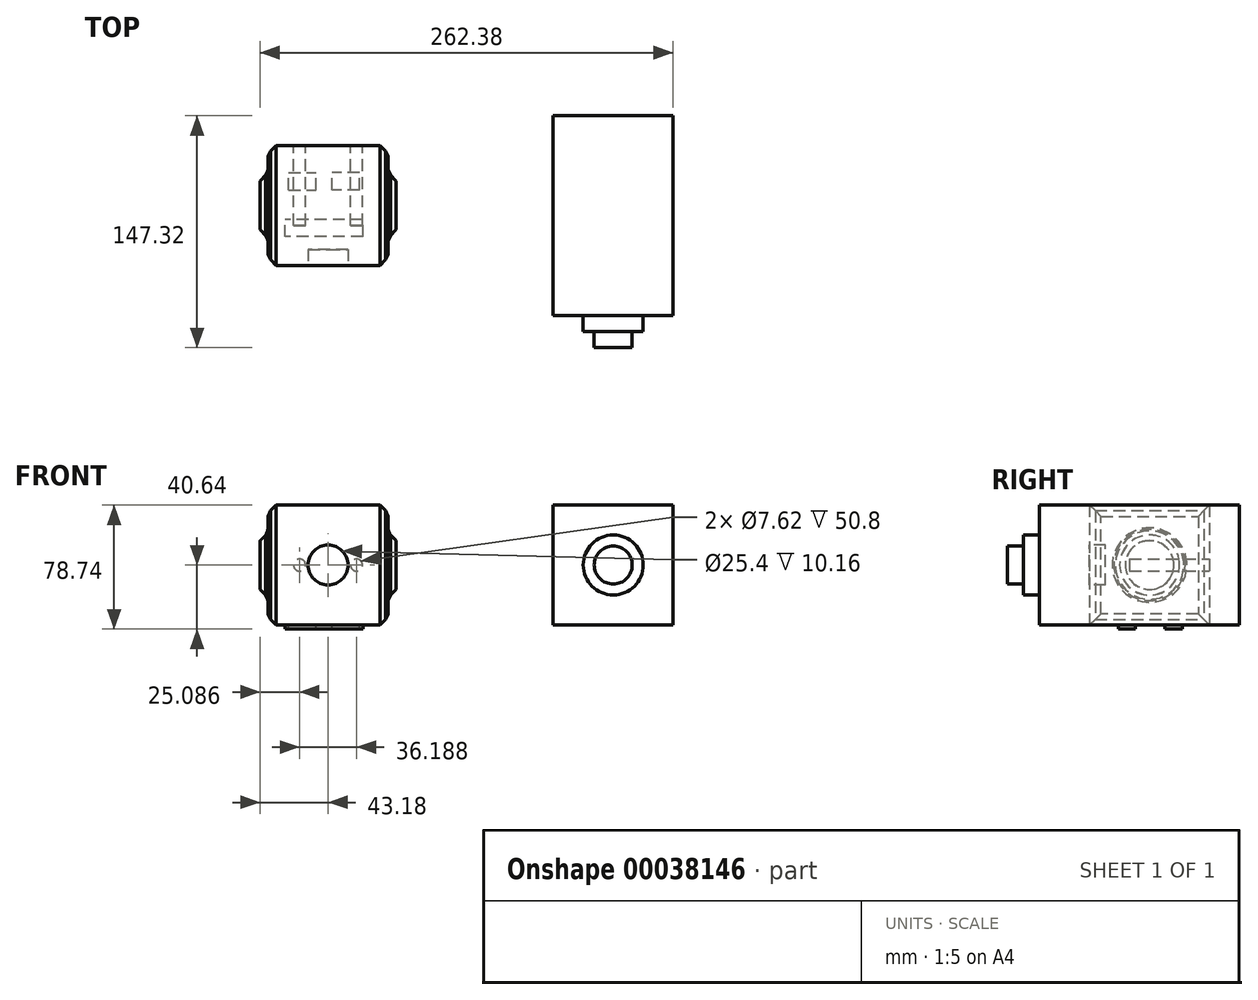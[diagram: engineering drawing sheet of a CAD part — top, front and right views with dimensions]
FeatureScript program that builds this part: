
annotation { "Feature Type Name" : "Feature", "Feature Type Description" : "" }
export const myFeature = defineFeature(function(context is Context, id is Id, definition is map)
    precondition{}
    {
        {
            var Q0;
            Q0=qCreatedBy(makeId("Top.planeOp"),FACE);
            var sketch = newSketch(context, id + "F0", { "sketchPlane" : qUnion([Q0])});
            skLineSegment(sketch, "E0.rect.bottom", {"start": v(-38.1, -38.1) * mm, "end": v(38.1, -38.1) * mm});
            skLineSegment(sketch, "E0.rect.top", {"start": v(-38.1, 38.1) * mm, "end": v(38.1, 38.1) * mm});
            skLineSegment(sketch, "E0.rect.left", {"start": v(-38.1, -38.1) * mm, "end": v(-38.1, -12.7) * mm});
            skLineSegment(sketch, "E0.rect.right", {"start": v(38.1, -38.1) * mm, "end": v(38.1, -12.7) * mm});
            skPoint(sketch, "E0.rect.middle", {"position": v(0, 0) * mm});
            skPoint(sketch, "E1", {"position": v(-38.1, -12.7) * mm});
            skPoint(sketch, "E2.endSnap0", {"position": v(-38.1, 0) * mm});
            skPoint(sketch, "E2.start.orphan", {"position": v(-38.1, 0) * mm});
            skLineSegment(sketch, "E3.trimOffspring", {"start": v(-38.1, 38.1) * mm, "end": v(-38.1, 38.1) * mm});
            skPoint(sketch, "E4.orphan", {"position": v(0, 38.1) * mm});
            skLineSegment(sketch, "E5.trimOffspring", {"start": v(38.1, 38.1) * mm, "end": v(38.1, 38.1) * mm});
            skPoint(sketch, "E6.end.orphan", {"position": v(0, -38.1) * mm});
            skPoint(sketch, "E7.rect.right.end.orphan", {"position": v(-50.16, 8.42) * mm});
            skPoint(sketch, "E8.orphan", {"position": v(-50.16, -8.42) * mm});
            skLineSegment(sketch, "E9", {"start": v(-38.1, 38.1) * mm, "end": v(-38.1, -12.7) * mm});
            skLineSegment(sketch, "E10", {"start": v(38.1, 38.1) * mm, "end": v(38.1, -12.7) * mm});
            skSolve(sketch);
        }
        {
            var Q0;
            Q0 = qSketchRegion(id + "F0", true);
            extrude(context, id + "F1", {"entities" : qUnion([Q0]), "depth" : 76.2 * mm});
        }
        {
            var Q0;
            Q0=makeQuery(id+"F1.opExtrude","SWEPT_FACE",FACE,{"disambiguationData":[OSD([sQuery(id+"F0.wireOp",EDGE,"E0.rect.right"),sQuery(id+"F0.wireOp",EDGE,"E5.trimOffspring"),sQuery(id+"F0.wireOp",EDGE,"E10")])]});
            var sketch = newSketch(context, id + "F2", { "sketchPlane" : qUnion([Q0])});
            skLineSegment(sketch, "E11.rect.bottom", {"start": v(-25.4, 12.7) * mm, "end": v(25.4, 12.7) * mm});
            skLineSegment(sketch, "E11.rect.top", {"start": v(-25.4, 63.5) * mm, "end": v(25.4, 63.5) * mm});
            skLineSegment(sketch, "E11.rect.left", {"start": v(-25.4, 12.7) * mm, "end": v(-25.4, 63.5) * mm});
            skLineSegment(sketch, "E11.rect.right", {"start": v(25.4, 12.7) * mm, "end": v(25.4, 63.5) * mm});
            skPoint(sketch, "E11.rect.middle", {"position": v(0, 38.1) * mm});
            skPoint(sketch, "E12.start.orphan", {"position": v(0, 76.2) * mm});
            skPoint(sketch, "E13.trimOffspring.end.orphan", {"position": v(0, 0) * mm});
            skSolve(sketch);
        }
        {
            var Q0;
            Q0=makeQuery(id+"FmdpoKRVJmVcfqV_1.opExtrude","SWEPT_FACE",FACE,{"disambiguationData":[OSD([sQuery(id+"F2.wireOp",EDGE,"E11.rect.bottom")])]});
            var Q1;
            Q1=makeQuery(id+"F1.opExtrude","SWEPT_FACE",FACE,{"disambiguationData":[OSD([sQuery(id+"F0.wireOp",EDGE,"E0.rect.right"),sQuery(id+"F0.wireOp",EDGE,"E5.trimOffspring"),sQuery(id+"F0.wireOp",EDGE,"E10")])]});
            var Q2;
            Q2=makeQuery(id+"FmdpoKRVJmVcfqV_1.opExtrude","SWEPT_FACE",FACE,{"disambiguationData":[OSD([sQuery(id+"F2.wireOp",EDGE,"E11.rect.left")])]});
            var Q3;
            Q3=makeQuery(id+"FmdpoKRVJmVcfqV_1.opExtrude","SWEPT_FACE",FACE,{"disambiguationData":[OSD([sQuery(id+"F2.wireOp",EDGE,"E11.rect.top")])]});
            var Q4;
            Q4=makeQuery(id+"FmdpoKRVJmVcfqV_1.opExtrude","SWEPT_FACE",FACE,{"disambiguationData":[OSD([sQuery(id+"F2.wireOp",EDGE,"E11.rect.right")])]});
            chamfer(context, id + "F3", {"entities" : qUnion([Q0, Q1, Q2, Q3, Q4]), "width" : 5.08 * mm, "tangentPropagation" : true});
        }
        {
            var Q0;
            Q0=makeQuery(id+"F1.opExtrude","SWEPT_FACE",FACE,{"disambiguationData":[OSD([sQuery(id+"F0.wireOp",EDGE,"E0.rect.left"),sQuery(id+"F0.wireOp",EDGE,"E3.trimOffspring"),sQuery(id+"F0.wireOp",EDGE,"E9")])]});
            var sketch = newSketch(context, id + "F4", { "sketchPlane" : qUnion([Q0])});
            skLineSegment(sketch, "E14", {"start": v(0, 76.2) * mm, "end": v(0, 0) * mm});
            skLineSegment(sketch, "E15.rect.bottom", {"start": v(-25.4, 12.7) * mm, "end": v(25.4, 12.7) * mm});
            skLineSegment(sketch, "E15.rect.top", {"start": v(-25.4, 63.5) * mm, "end": v(25.4, 63.5) * mm});
            skLineSegment(sketch, "E15.rect.left", {"start": v(-25.4, 12.7) * mm, "end": v(-25.4, 63.5) * mm});
            skLineSegment(sketch, "E15.rect.right", {"start": v(25.4, 12.7) * mm, "end": v(25.4, 63.5) * mm});
            skPoint(sketch, "E15.rect.middle", {"position": v(0, 38.1) * mm});
            skSolve(sketch);
        }
        {
            var Q0;
            Q0=makeQuery(id+"F1.opExtrude","SWEPT_FACE",FACE,{"disambiguationData":[OSD([sQuery(id+"F0.wireOp",EDGE,"E0.rect.top")])]});
            var sketch = newSketch(context, id + "F5", { "sketchPlane" : qUnion([Q0])});
            skLineSegment(sketch, "E16", {"start": v(-21.9, 38.1) * mm, "end": v(-14.28, 38.1) * mm});
            skCircle(sketch, "E17", {"center": v(-18.1, 38.1) * mm, "radius": 3.81 * mm});
            skCircle(sketch, "E18.MirrorC", {"center": v(18.1, 38.1) * mm, "radius": 3.81 * mm});
            skPoint(sketch, "E19.start.orphan", {"position": v(0, 38.1) * mm});
            skLineSegment(sketch, "E20.trimOffspring", {"start": v(14.28, 38.1) * mm, "end": v(21.9, 38.1) * mm});
            skPoint(sketch, "E21.orphan", {"position": v(-33.02, 38.1) * mm});
            skPoint(sketch, "E22.orphan", {"position": v(33.02, 38.1) * mm});
            skSolve(sketch);
        }
        {
            var Q0;
            Q0 = qSketchRegion(id + "F5", true);
            extrude(context, id + "F6", {"entities" : qUnion([Q0]), "operationType" : NewBodyOperationType.REMOVE, "oppositeDirection" : true, "depth" : 50.8 * mm});
        }
        {
            var Q0;
            Q0=makeQuery(id+"F1.opExtrude","CAP_FACE",FACE,{"disambiguationData":[OSD([sQuery(id+"F0.wireOp",EDGE,"E0.rect.bottom"),sQuery(id+"F0.wireOp",EDGE,"E0.rect.top"),sQuery(id+"F0.wireOp",EDGE,"E0.rect.left"),sQuery(id+"F0.wireOp",EDGE,"E0.rect.right"),sQuery(id+"F0.wireOp",EDGE,"E9"),sQuery(id+"F0.wireOp",EDGE,"E10")])],"isStart":true});
            var sketch = newSketch(context, id + "F7", { "sketchPlane" : qUnion([Q0])});
            skPoint(sketch, "E23.start.orphan", {"position": v(-2.54, -38.1) * mm});
            skLineSegment(sketch, "E24", {"start": v(-2.54, -38.1) * mm, "end": v(-2.54, 38.1) * mm});
            skLineSegment(sketch, "E25.rect.bottom", {"start": v(19.99, -9.73) * mm, "end": v(2.65, -9.73) * mm});
            skLineSegment(sketch, "E25.rect.top", {"start": v(19.99, -20.71) * mm, "end": v(2.65, -20.71) * mm});
            skLineSegment(sketch, "E25.rect.left", {"start": v(19.99, -9.73) * mm, "end": v(19.99, -20.71) * mm});
            skLineSegment(sketch, "E25.rect.right", {"start": v(2.65, -9.73) * mm, "end": v(2.65, -20.71) * mm});
            skPoint(sketch, "E25.rect.middle", {"position": v(11.32, -15.22) * mm});
            skLineSegment(sketch, "E26.MirrorCS", {"start": v(-7.73, -9.73) * mm, "end": v(-7.73, -20.71) * mm});
            skPoint(sketch, "E27.MirrorP", {"position": v(-16.4, -15.22) * mm});
            skLineSegment(sketch, "E28.MirrorCS", {"start": v(-25.07, -9.73) * mm, "end": v(-25.07, -20.71) * mm});
            skLineSegment(sketch, "E29.MirrorCS", {"start": v(-25.07, -9.73) * mm, "end": v(-7.73, -9.73) * mm});
            skLineSegment(sketch, "E30.MirrorCS", {"start": v(-25.07, -20.71) * mm, "end": v(-7.73, -20.71) * mm});
            skLineSegment(sketch, "E31.rect.bottom", {"start": v(22.06, 19.9) * mm, "end": v(-27.14, 19.9) * mm});
            skLineSegment(sketch, "E31.rect.top", {"start": v(22.06, 8.92) * mm, "end": v(-27.14, 8.92) * mm});
            skLineSegment(sketch, "E31.rect.left", {"start": v(22.06, 19.9) * mm, "end": v(22.06, 8.92) * mm});
            skLineSegment(sketch, "E31.rect.right", {"start": v(-27.14, 19.9) * mm, "end": v(-27.14, 8.92) * mm});
            skPoint(sketch, "E31.rect.middle", {"position": v(-2.54, 14.41) * mm});
            skSolve(sketch);
        }
        {
            var Q0;
            Q0 = qSketchRegion(id + "F7", true);
            extrude(context, id + "F8", {"entities" : qUnion([Q0]), "operationType" : NewBodyOperationType.ADD, "depth" : 2.54 * mm});
        }
        {
            var Q0;
            Q0=makeQuery(id+"F1.opExtrude","SWEPT_FACE",FACE,{"disambiguationData":[OSD([sQuery(id+"F0.wireOp",EDGE,"E0.rect.left"),sQuery(id+"F0.wireOp",EDGE,"E9")])]});
            chamfer(context, id + "F9", {"entities" : qUnion([Q0]), "width" : 5.08 * mm, "tangentPropagation" : true});
        }
        {
            var Q0;
            {var subQ0=sQuery(id+"F4.wireOp",EDGE,"E15.rect.left");Q0=makeQuery(id+"F4.imprint","IMPRINT",FACE,{"disambiguationData":[TD([[makeQuery(id+"F4.imprint","IMPRINT",EDGE,{"derivedFrom":subQ0}),-1.0]])]});}
            var sketch = newSketch(context, id + "F10", { "sketchPlane" : qUnion([Q0])});
            skPoint(sketch, "E32.rect.middle", {"position": v(0, 36.06) * mm});
            skPoint(sketch, "E33.orphan", {"position": v(0, 67.25) * mm});
            skPoint(sketch, "E34.end.orphan", {"position": v(0, 4.86) * mm});
            skPoint(sketch, "E32.rect.top.start.orphan", {"position": v(-12.7, 48.76) * mm});
            skPoint(sketch, "E32.rect.right.end.orphan", {"position": v(12.7, 48.76) * mm});
            skPoint(sketch, "E32.rect.bottom.end.orphan", {"position": v(12.7, 23.36) * mm});
            skPoint(sketch, "E32.rect.bottom.start.orphan", {"position": v(-12.7, 23.36) * mm});
            skLineSegment(sketch, "E35", {"start": v(0, 71.25) * mm, "end": v(0, 4.86) * mm});
            skCircle(sketch, "E36", {"center": v(0, 38.06) * mm, "radius": 15.48 * mm});
            skSolve(sketch);
        }
        {
            var Q0;
            Q0 = qSketchRegion(id + "F10", true);
            extrude(context, id + "F11", {"entities" : qUnion([Q0]), "operationType" : NewBodyOperationType.ADD, "depth" : 5.08 * mm});
        }
        {
            var Q0;
            Q0=makeQuery(id+"F1.opExtrude","SWEPT_FACE",FACE,{"disambiguationData":[OSD([sQuery(id+"F0.wireOp",EDGE,"E0.rect.left"),sQuery(id+"F0.wireOp",EDGE,"E9")])]});
            chamfer(context, id + "F12", {"entities" : qUnion([Q0]), "width" : 5.08 * mm, "tangentPropagation" : true});
        }
        {
            var Q0;
            Q0=makeQuery(id+"F2.imprint","IMPRINT",FACE,{"disambiguationData":[TD([[makeQuery(id+"F2.imprint","IMPRINT",EDGE,{"derivedFrom":sQuery(id+"F2.wireOp",EDGE,"E11.rect.bottom")}),1.0]])]});
            var sketch = newSketch(context, id + "F13", { "sketchPlane" : qUnion([Q0])});
            skCircle(sketch, "E37", {"center": v(0, 38.13) * mm, "radius": 15.48 * mm});
            skPoint(sketch, "E38.orphan", {"position": v(0, 72.13) * mm});
            skPoint(sketch, "E39.end.orphan", {"position": v(0, 4.14) * mm});
            skSolve(sketch);
        }
        {
            var Q0;
            Q0 = qSketchRegion(id + "F13", true);
            extrude(context, id + "F14", {"entities" : qUnion([Q0]), "operationType" : NewBodyOperationType.ADD, "depth" : 5.08 * mm});
        }
        {
            var Q0;
            Q0=makeQuery(id+"F1.opExtrude","SWEPT_FACE",FACE,{"disambiguationData":[OSD([sQuery(id+"F0.wireOp",EDGE,"E0.rect.right"),sQuery(id+"F0.wireOp",EDGE,"E10")])]});
            chamfer(context, id + "F15", {"entities" : qUnion([Q0]), "width" : 5.08 * mm, "tangentPropagation" : true});
        }
        {
            var Q0;
            Q0=makeQuery(id+"F1.opExtrude","SWEPT_FACE",FACE,{"disambiguationData":[OSD([sQuery(id+"F0.wireOp",EDGE,"E0.rect.bottom")])]});
            var sketch = newSketch(context, id + "F16", { "sketchPlane" : qUnion([Q0])});
            skLineSegment(sketch, "E40", {"start": v(-33.02, 38.1) * mm, "end": v(33.02, 38.1) * mm});
            skCircle(sketch, "E41", {"center": v(0, 38.1) * mm, "radius": 12.7 * mm});
            skSolve(sketch);
        }
        {
            var Q0;
            Q0 = qSketchRegion(id + "F16", true);
            extrude(context, id + "F17", {"entities" : qUnion([Q0]), "operationType" : NewBodyOperationType.REMOVE, "oppositeDirection" : true, "depth" : 10.16 * mm});
        }
        {
            var Q0;
            Q0=qCreatedBy(makeId("Top.planeOp"),FACE);
            var sketch = newSketch(context, id + "F18", { "sketchPlane" : qUnion([Q0])});
            skLineSegment(sketch, "E42.rect.bottom", {"start": v(219.2, -70.07) * mm, "end": v(143, -70.07) * mm});
            skLineSegment(sketch, "E42.rect.top", {"start": v(193.8, 56.93) * mm, "end": v(168.4, 56.93) * mm});
            skLineSegment(sketch, "E42.rect.left", {"start": v(219.2, -70.07) * mm, "end": v(219.2, 25.45) * mm});
            skLineSegment(sketch, "E42.rect.right", {"start": v(143, -70.07) * mm, "end": v(143, 25.45) * mm});
            skPoint(sketch, "E42.rect.middle", {"position": v(181.1, -6.57) * mm});
            skLineSegment(sketch, "E43.rect.left", {"start": v(193.8, 56.93) * mm, "end": v(193.8, 25.45) * mm});
            skLineSegment(sketch, "E43.rect.right", {"start": v(168.4, 56.93) * mm, "end": v(168.4, 25.45) * mm});
            skPoint(sketch, "E43.rect.middle", {"position": v(181.1, 56.93) * mm});
            skPoint(sketch, "E43.rect.bottom.end.orphan", {"position": v(168.4, 88.42) * mm});
            skPoint(sketch, "E43.rect.bottom.start.orphan", {"position": v(193.8, 88.42) * mm});
            skLineSegment(sketch, "E44", {"start": v(168.4, 25.45) * mm, "end": v(143, 25.45) * mm});
            skLineSegment(sketch, "E45", {"start": v(193.8, 25.45) * mm, "end": v(219.2, 25.45) * mm});
            skPoint(sketch, "E46.orphan", {"position": v(143, 56.93) * mm});
            skPoint(sketch, "E47.orphan", {"position": v(219.2, 56.93) * mm});
            skLineSegment(sketch, "E48.top", {"start": v(168.4, 56.93) * mm, "end": v(143, 56.93) * mm});
            skLineSegment(sketch, "E48.left", {"start": v(168.4, 25.45) * mm, "end": v(168.4, 56.93) * mm});
            skLineSegment(sketch, "E48.right", {"start": v(143, 25.45) * mm, "end": v(143, 56.93) * mm});
            skLineSegment(sketch, "E49.top", {"start": v(193.8, 56.93) * mm, "end": v(219.2, 56.93) * mm});
            skLineSegment(sketch, "E49.left", {"start": v(193.8, 25.45) * mm, "end": v(193.8, 56.93) * mm});
            skLineSegment(sketch, "E49.right", {"start": v(219.2, 25.45) * mm, "end": v(219.2, 56.93) * mm});
            skSolve(sketch);
        }
        {
            var Q0;
            Q0 = qSketchRegion(id + "F18", true);
            extrude(context, id + "F19", {"entities" : qUnion([Q0]), "depth" : 76.2 * mm});
        }
        {
            var Q0;
            Q0=makeQuery(id+"F19.opExtrude","SWEPT_FACE",FACE,{"disambiguationData":[OSD([sQuery(id+"F18.wireOp",EDGE,"E42.rect.bottom")])]});
            var sketch = newSketch(context, id + "F20", { "sketchPlane" : qUnion([Q0])});
            skLineSegment(sketch, "E50", {"start": v(143, 38.1) * mm, "end": v(219.2, 38.1) * mm});
            skCircle(sketch, "E51", {"center": v(181.1, 38.1) * mm, "radius": 12.07 * mm});
            skCircle(sketch, "E52", {"center": v(181.1, 38.1) * mm, "radius": 19.05 * mm});
            skSolve(sketch);
        }
        {
            var Q0;
            Q0 = qSketchRegion(id + "F20", true);
            extrude(context, id + "F21", {"entities" : qUnion([Q0]), "operationType" : NewBodyOperationType.ADD, "depth" : 10.16 * mm});
        }
        {
            var Q0;
            {var subQ0=sQuery(id+"F20.wireOp",EDGE,"E51");var subQ1=sQuery(id+"F20.wireOp",EDGE,"E50");var subQ3=makeQuery(id+"F20.imprint","INTERSECT",VERTEX,{"disambiguationData":[OD(0.0)],"derivedFrom":[subQ1,subQ0]});Q0=makeQuery(id+"F20.imprint","IMPRINT",FACE,{"disambiguationData":[TD([[makeQuery(id+"F20.imprint","IMPRINT",EDGE,{"disambiguationData":[TD([[subQ3,-1.0]])],"derivedFrom":subQ1}),1.0]])]});}
            var Q1;
            {var subQ0=sQuery(id+"F20.wireOp",EDGE,"E51");var subQ1=sQuery(id+"F20.wireOp",EDGE,"E50");var subQ3=makeQuery(id+"F20.imprint","INTERSECT",VERTEX,{"disambiguationData":[OD(0.0)],"derivedFrom":[subQ1,subQ0]});Q1=makeQuery(id+"F20.imprint","IMPRINT",FACE,{"disambiguationData":[TD([[makeQuery(id+"F20.imprint","IMPRINT",EDGE,{"disambiguationData":[TD([[subQ3,-1.0]])],"derivedFrom":subQ1}),-1.0]])]});}
            extrude(context, id + "F22", {"entities" : qUnion([Q0, Q1]), "operationType" : NewBodyOperationType.ADD, "depth" : 20.32 * mm});
        }
    });
